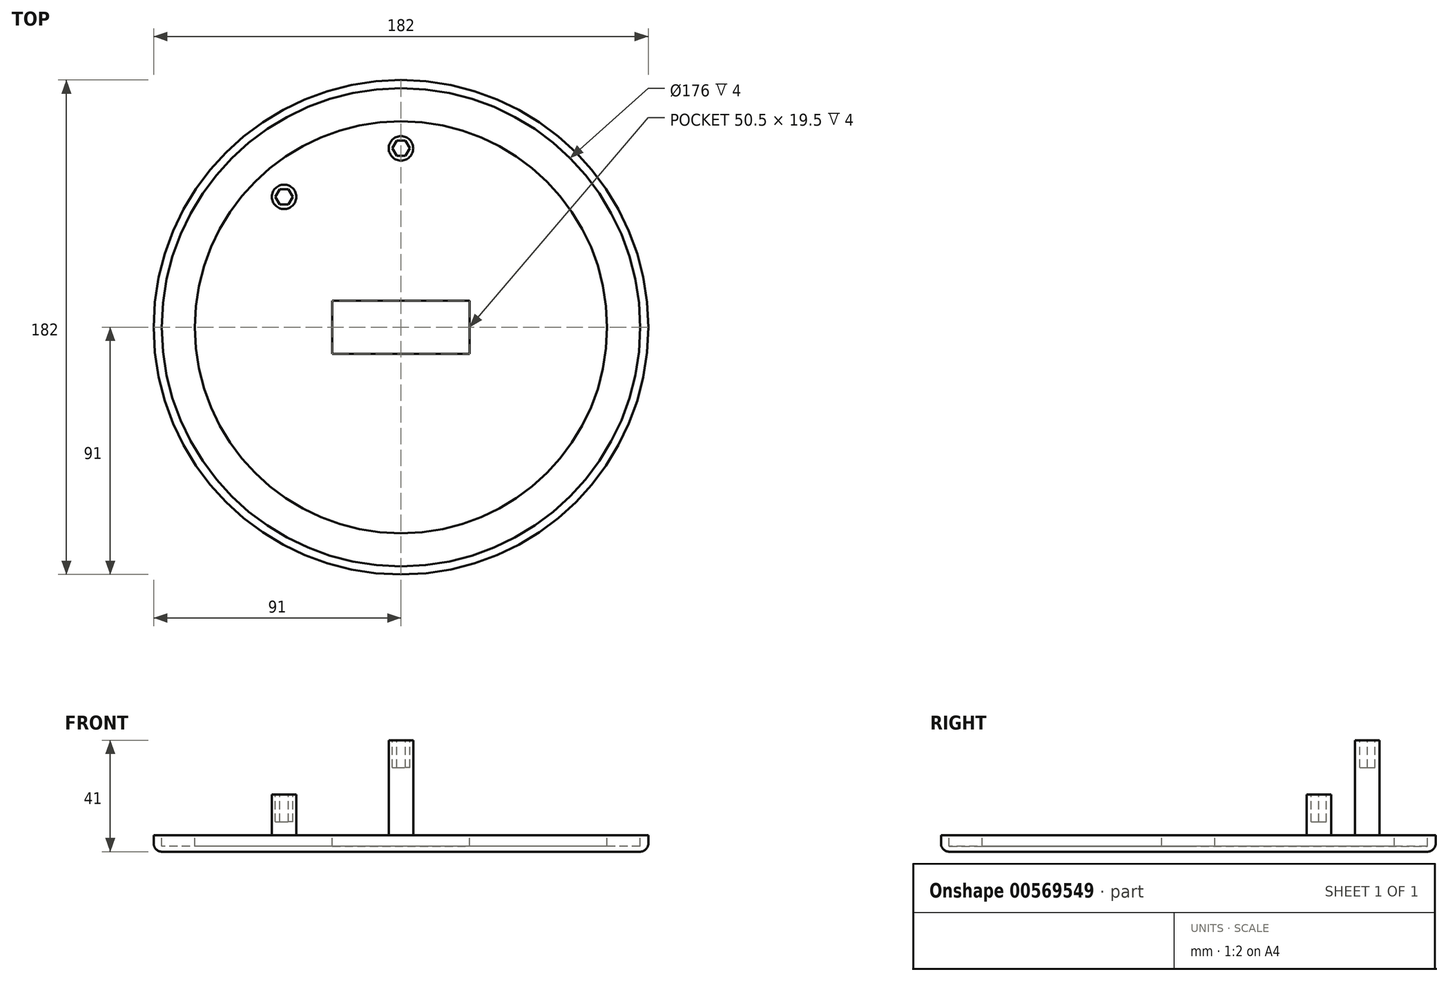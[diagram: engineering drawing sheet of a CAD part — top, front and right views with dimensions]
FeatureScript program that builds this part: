
annotation { "Feature Type Name" : "Feature", "Feature Type Description" : "" }
export const myFeature = defineFeature(function(context is Context, id is Id, definition is map)
    precondition{}
    {
        {
            var Q0;
            Q0=qCreatedBy(makeId("Top.planeOp"),FACE);
            var sketch = newSketch(context, id + "F0", { "sketchPlane" : qUnion([Q0])});
            skCircle(sketch, "E0", {"center": v(0, 0) * mm, "radius": 91 * mm});
            skSolve(sketch);
        }
        {
            var Q0;
            Q0=makeQuery(id+"F0.imprint","IMPRINT",FACE,{"disambiguationData":[TD([[makeQuery(id+"F0.imprint","IMPRINT",EDGE,{"derivedFrom":sQuery(id+"F0.wireOp",EDGE,"E0")}),1.0]])]});
            var Q1;
            Q1=sQuery(id+"F0.wireOp",EDGE,"E0");
            extrude(context, id + "F1", {"entities" : qUnion([Q0]), "surfaceEntities" : qUnion([Q1]), "depth" : 6 * mm, "offsetDistance" : 25 * mm});
        }
        {
            var Q0;
            Q0=makeQuery(id+"F1.opExtrude","CAP_FACE",FACE,{"disambiguationData":[OSD([sQuery(id+"F0.wireOp",EDGE,"E0")])],"isStart":false});
            var sketch = newSketch(context, id + "F2", { "sketchPlane" : qUnion([Q0])});
            skCircle(sketch, "E1", {"center": v(0, 0) * mm, "radius": 88 * mm});
            skSolve(sketch);
        }
        {
            var Q0;
            Q0=makeQuery(id+"F2.imprint","IMPRINT",FACE,{"disambiguationData":[TD([[makeQuery(id+"F2.imprint","IMPRINT",EDGE,{"derivedFrom":sQuery(id+"F2.wireOp",EDGE,"E1")}),-1.0]])]});
            var sketch = newSketch(context, id + "F3", { "sketchPlane" : qUnion([Q0])});
            skCircle(sketch, "E2", {"center": v(0, 0) * mm, "radius": 75.85 * mm});
            skSolve(sketch);
        }
        {
            var Q0;
            Q0=makeQuery(id+"F3.imprint","IMPRINT",FACE,{"disambiguationData":[TD([[makeQuery(id+"F3.imprint","IMPRINT",EDGE,{"derivedFrom":sQuery(id+"F3.wireOp",EDGE,"E2")}),-1.0]])]});
            var Q1;
            Q1=sQuery(id+"F2.wireOp",EDGE,"E1");
            var Q2;
            Q2=sQuery(id+"F3.wireOp",EDGE,"E2");
            extrude(context, id + "F4", {"entities" : qUnion([Q0]), "operationType" : NewBodyOperationType.REMOVE, "surfaceEntities" : qUnion([Q1, Q2]), "oppositeDirection" : true, "depth" : 4 * mm, "offsetDistance" : 25 * mm});
        }
        {
            var Q0;
            Q0=makeQuery(id+"F4.boolean.opBoolean","SPLIT",FACE,{"disambiguationData":[TD([makeQuery(id+"F4.opExtrude","SWEPT_FACE",FACE,{"disambiguationData":[OSD([sQuery(id+"F3.wireOp",EDGE,"E2")])]})])],"derivedFrom":makeQuery(id+"F1.opExtrude","CAP_FACE",FACE,{"disambiguationData":[OSD([sQuery(id+"F0.wireOp",EDGE,"E0")])],"isStart":false})});
            var sketch = newSketch(context, id + "F5", { "sketchPlane" : qUnion([Q0])});
            skLineSegment(sketch, "E3.bottom", {"start": v(-25.25, 9.75) * mm, "end": v(25.25, 9.75) * mm});
            skLineSegment(sketch, "E3.top", {"start": v(-25.25, -9.75) * mm, "end": v(25.25, -9.75) * mm});
            skLineSegment(sketch, "E3.left", {"start": v(-25.25, 9.75) * mm, "end": v(-25.25, -9.75) * mm});
            skLineSegment(sketch, "E3.right", {"start": v(25.25, 9.75) * mm, "end": v(25.25, -9.75) * mm});
            skPoint(sketch, "E3.middle", {"position": v(0, 0) * mm});
            skSolve(sketch);
        }
        {
            var Q0;
            Q0=qSketchRegion(id+"F5",true);
            extrude(context, id + "F6", {"entities" : qUnion([Q0]), "operationType" : NewBodyOperationType.REMOVE, "oppositeDirection" : true, "depth" : 4 * mm, "offsetDistance" : 25 * mm});
        }
        {
            var Q0;
            Q0=makeQuery(id+"FstaHTkGCtETjQ8_1.boolean.opBoolean","SPLIT",FACE,{"disambiguationData":[TD([makeQuery(id+"F6.boolean.opBoolean","COPY",FACE,{"derivedFrom":makeQuery(id+"F6.opExtrude","SWEPT_FACE",FACE,{"disambiguationData":[OSD([sQuery(id+"F5.wireOp",EDGE,"E3.bottom")])]})})])],"derivedFrom":makeQuery(id+"F4.boolean.opBoolean","SPLIT",FACE,{"disambiguationData":[TD([makeQuery(id+"F4.opExtrude","SWEPT_FACE",FACE,{"disambiguationData":[OSD([sQuery(id+"F3.wireOp",EDGE,"E2")])]})])],"derivedFrom":makeQuery(id+"F1.opExtrude","CAP_FACE",FACE,{"disambiguationData":[OSD([sQuery(id+"F0.wireOp",EDGE,"E0")])],"isStart":false})})});
            var sketch = newSketch(context, id + "F7", { "sketchPlane" : qUnion([Q0])});
            skLineSegment(sketch, "E4.bottom", {"start": v(-48, 53) * mm, "end": v(48, 53) * mm});
            skLineSegment(sketch, "E4.top", {"start": v(-48, -53) * mm, "end": v(48, -53) * mm});
            skLineSegment(sketch, "E4.left", {"start": v(-48, 53) * mm, "end": v(-48, -53) * mm});
            skLineSegment(sketch, "E4.right", {"start": v(48, 53) * mm, "end": v(48, -53) * mm});
            skPoint(sketch, "E4.middle", {"position": v(0, 0) * mm});
            skSolve(sketch);
        }
        {
            var Q0;
            Q0=makeQuery(id+"F7.imprint","IMPRINT",FACE,{"disambiguationData":[TD([[makeQuery(id+"F7.imprint","IMPRINT",EDGE,{"derivedFrom":sQuery(id+"F7.wireOp",EDGE,"E4.bottom")}),1.0]])]});
            var sketch = newSketch(context, id + "F8", { "sketchPlane" : qUnion([Q0])});
            skCircle(sketch, "E5", {"center": v(0, 65.85) * mm, "radius": 4.5 * mm});
            skSolve(sketch);
        }
        {
            var Q0;
            Q0=qSketchRegion(id+"F8",true);
            extrude(context, id + "F9", {"entities" : qUnion([Q0]), "operationType" : NewBodyOperationType.ADD, "depth" : 35 * mm, "offsetDistance" : 25 * mm});
        }
        {
            var Q0;
            Q0=makeQuery(id+"F9.opExtrude","CAP_FACE",FACE,{"disambiguationData":[OSD([sQuery(id+"F8.wireOp",EDGE,"E5")])],"isStart":false});
            var sketch = newSketch(context, id + "F10", { "sketchPlane" : qUnion([Q0])});
            skCircle(sketch, "E6.cCircle", {"center": v(0, 65.85) * mm, "radius": 3.23 * mm, "construction": true});
            skLineSegment(sketch, "E6.0", {"start": v(-1.62, 68.65) * mm, "end": v(1.62, 68.65) * mm});
            skLineSegment(sketch, "E6.1", {"start": v(1.62, 68.65) * mm, "end": v(3.23, 65.85) * mm});
            skLineSegment(sketch, "E6.2", {"start": v(3.23, 65.85) * mm, "end": v(1.62, 63.05) * mm});
            skLineSegment(sketch, "E6.3", {"start": v(1.62, 63.05) * mm, "end": v(-1.62, 63.05) * mm});
            skLineSegment(sketch, "E6.4", {"start": v(-1.62, 63.05) * mm, "end": v(-3.23, 65.85) * mm});
            skLineSegment(sketch, "E6.5", {"start": v(-3.23, 65.85) * mm, "end": v(-1.62, 68.65) * mm});
            skSolve(sketch);
        }
        {
            var Q0;
            Q0=makeQuery(id+"F10.imprint","IMPRINT",FACE,{"disambiguationData":[TD([[makeQuery(id+"F10.imprint","IMPRINT",EDGE,{"derivedFrom":sQuery(id+"F10.wireOp",EDGE,"E6.0")}),-1.0]])]});
            extrude(context, id + "F11", {"entities" : qUnion([Q0]), "operationType" : NewBodyOperationType.REMOVE, "oppositeDirection" : true, "depth" : 10 * mm, "offsetDistance" : 25 * mm});
        }
        {
            var Q0;
            Q0=makeQuery(id+"F7.imprint","IMPRINT",FACE,{"disambiguationData":[TD([[makeQuery(id+"F7.imprint","IMPRINT",EDGE,{"derivedFrom":sQuery(id+"F7.wireOp",EDGE,"E4.bottom")}),-1.0]])]});
            var sketch = newSketch(context, id + "F12", { "sketchPlane" : qUnion([Q0])});
            skCircle(sketch, "E7", {"center": v(-43, 48) * mm, "radius": 4.5 * mm});
            skSolve(sketch);
        }
        {
            var Q0;
            Q0 = qSketchRegion(id + "F12", true);
            extrude(context, id + "F13", {"entities" : qUnion([Q0]), "operationType" : NewBodyOperationType.ADD, "depth" : 15 * mm, "offsetDistance" : 25 * mm});
        }
        {
            var Q0;
            Q0=makeQuery(id+"F13.opExtrude","CAP_FACE",FACE,{"disambiguationData":[OSD([sQuery(id+"F12.wireOp",EDGE,"E7")])],"isStart":false});
            var sketch = newSketch(context, id + "F14", { "sketchPlane" : qUnion([Q0])});
            skCircle(sketch, "E8.cCircle", {"center": v(-43, 48) * mm, "radius": 3.23 * mm, "construction": true});
            skLineSegment(sketch, "E8.0", {"start": v(-44.62, 50.8) * mm, "end": v(-41.38, 50.8) * mm});
            skLineSegment(sketch, "E8.1", {"start": v(-41.38, 50.8) * mm, "end": v(-39.77, 48) * mm});
            skLineSegment(sketch, "E8.2", {"start": v(-39.77, 48) * mm, "end": v(-41.38, 45.2) * mm});
            skLineSegment(sketch, "E8.3", {"start": v(-41.38, 45.2) * mm, "end": v(-44.62, 45.2) * mm});
            skLineSegment(sketch, "E8.4", {"start": v(-44.62, 45.2) * mm, "end": v(-46.23, 48) * mm});
            skLineSegment(sketch, "E8.5", {"start": v(-46.23, 48) * mm, "end": v(-44.62, 50.8) * mm});
            skSolve(sketch);
        }
        {
            var Q0;
            Q0 = qSketchRegion(id + "F14", true);
            extrude(context, id + "F15", {"entities" : qUnion([Q0]), "operationType" : NewBodyOperationType.REMOVE, "oppositeDirection" : true, "depth" : 10 * mm, "offsetDistance" : 25 * mm});
        }
        {
            var Q0;
            Q0=makeQuery(id+"F1.opExtrude","CAP_EDGE",EDGE,{"disambiguationData":[OSD([sQuery(id+"F0.wireOp",EDGE,"E0")])],"isStart":true});
            fillet(context, id + "F16", {"entities" : qUnion([Q0]), "radius" : 3 * mm, "tangentPropagation" : true, "allowEdgeOverflow" : false});
        }
    });
